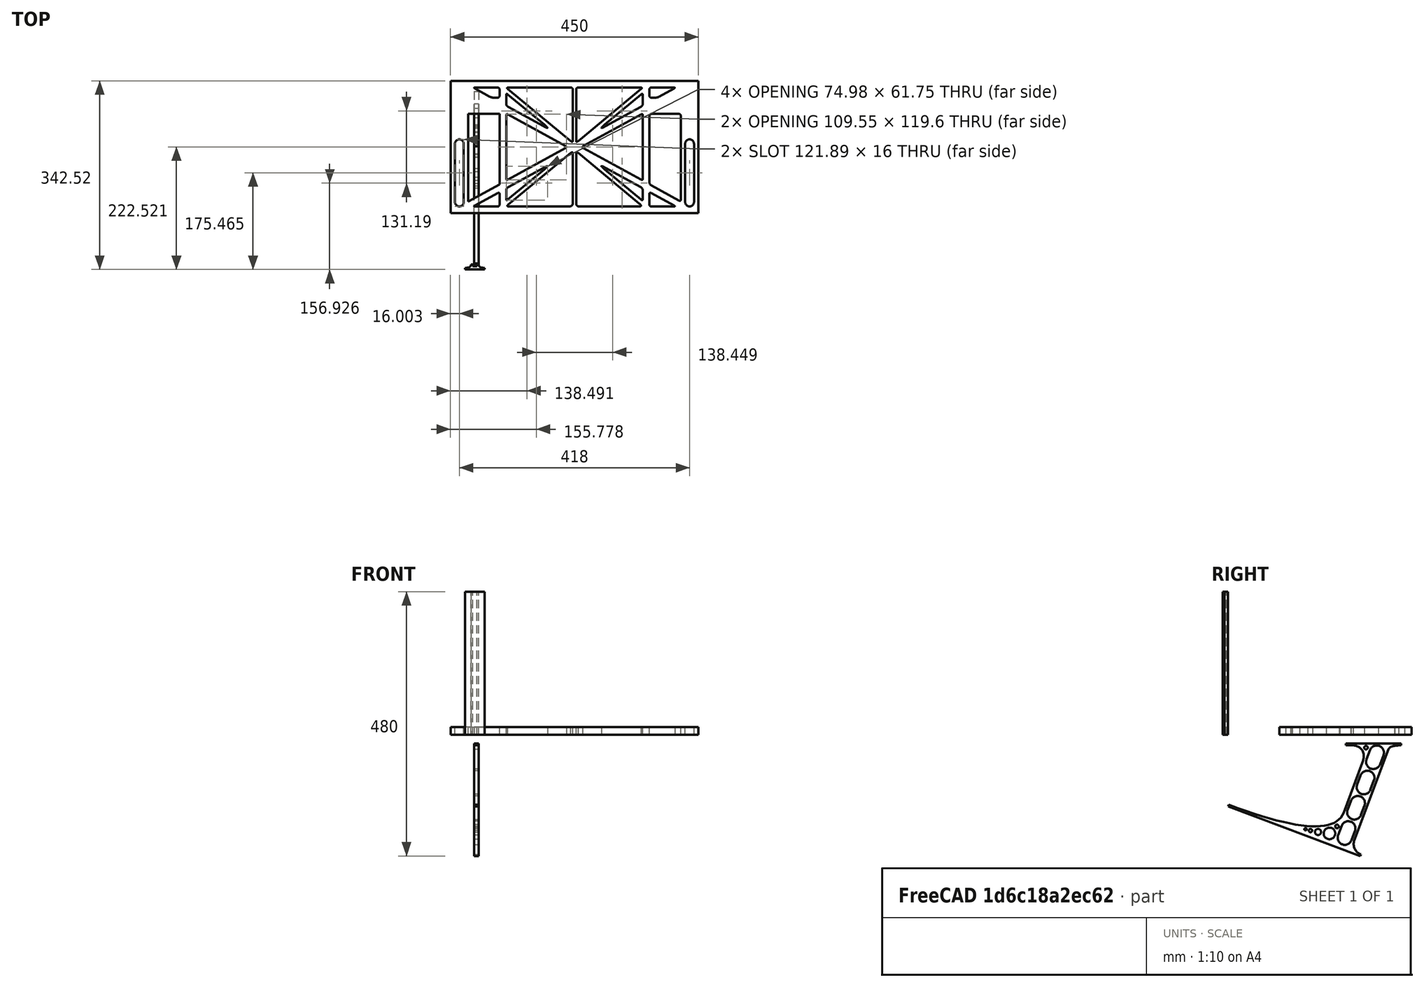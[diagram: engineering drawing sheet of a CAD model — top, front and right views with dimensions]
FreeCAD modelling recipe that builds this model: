
FCSTD DOCUMENT  (FreeCAD 0.19R0.19.2)
Label: laptopStand136FCStd
License: All rights reserved
LicenseURL: http://en.wikipedia.org/wiki/All_rights_reserved
objects: Sketcher::SketchObject×3, Part::Extrusion×3
note: 6 computed .brp shape members not serialized (recipe doc carries the construction recipe); baked Part::Feature solids carry a one-line shape summary decoded from their .brp

FEATURE [Sketcher::SketchObject] Sketch
  FullyConstrained = false
  sketch-geometry (352):
    g0: LineSegment StartX=-10.9272 StartY=-82.7794 StartZ=0 EndX=46.0728 EndY=-51.4823 EndZ=0
    g1: LineSegment StartX=-10.9272 StartY=76.4095 StartZ=0 EndX=-10.9272 EndY=-82.7794 EndZ=0
    g2: LineSegment StartX=46.0728 StartY=76.4095 StartZ=0 EndX=46.0728 EndY=-51.4823 EndZ=0
    g3: LineSegment StartX=-42.9272 StartY=136.221 StartZ=0 EndX=-42.9272 EndY=-103.779 EndZ=0
    g4: LineSegment StartX=407.073 StartY=136.221 StartZ=0 EndX=407.073 EndY=-103.779 EndZ=0
    g5: ArcOfCircle CenterX=-26.9272 CenterY=22.1087 CenterZ=0 NormalX=0 NormalY=0 NormalZ=1 AngleXU=0 Radius=8 StartAngle=3e-16 EndAngle=3.14159
    g6: ArcOfCircle CenterX=-26.9272 CenterY=-83.7794 CenterZ=0 NormalX=0 NormalY=0 NormalZ=1 AngleXU=0 Radius=8 StartAngle=3.14159 EndAngle=6.28319
    g7: LineSegment StartX=-34.9272 StartY=22.1087 StartZ=0 EndX=-34.9272 EndY=-83.7794 EndZ=0
    g8: LineSegment StartX=-18.9272 StartY=22.1087 StartZ=0 EndX=-18.9272 EndY=-83.7794 EndZ=0
    g9: ArcOfCircle CenterX=391.073 CenterY=22.1087 CenterZ=0 NormalX=0 NormalY=0 NormalZ=1 AngleXU=0 Radius=8 StartAngle=-4.4e-15 EndAngle=3.14159
    g10: LineSegment StartX=399.073 StartY=22.1087 StartZ=0 EndX=399.073 EndY=-83.7794 EndZ=0
    g11: LineSegment StartX=383.073 StartY=22.1087 StartZ=0 EndX=383.073 EndY=-83.7794 EndZ=0
    g12: ArcOfCircle CenterX=391.073 CenterY=-83.7794 CenterZ=0 NormalX=0 NormalY=0 NormalZ=1 AngleXU=0 Radius=8 StartAngle=3.14159 EndAngle=6.28319
    g13: Circle CenterX=175.022 CenterY=27.0628 CenterZ=0 NormalX=0 NormalY=0 NormalZ=1 AngleXU=0 Radius=1
    g14: Circle CenterX=179.022 CenterY=24.8665 CenterZ=0 NormalX=0 NormalY=0 NormalZ=1 AngleXU=0 Radius=1
    g15: Circle CenterX=179.022 CenterY=27.0628 CenterZ=0 NormalX=0 NormalY=0 NormalZ=1 AngleXU=0 Radius=1
    g16: BSplineCurve PolesCount=3 KnotsCount=2 Degree=2 IsPeriodic=0
    g17: GeomPoint X=175.022 Y=27.0628 Z=0
    g18: GeomPoint X=179.022 Y=27.0628 Z=0
    g19: Circle CenterX=189.124 CenterY=27.0628 CenterZ=0 NormalX=0 NormalY=0 NormalZ=1 AngleXU=0 Radius=1
    g20: Circle CenterX=185.124 CenterY=24.8665 CenterZ=0 NormalX=0 NormalY=0 NormalZ=1 AngleXU=0 Radius=1
    g21: Circle CenterX=185.124 CenterY=27.0628 CenterZ=0 NormalX=0 NormalY=0 NormalZ=1 AngleXU=0 Radius=1
    g22: BSplineCurve PolesCount=3 KnotsCount=2 Degree=2 IsPeriodic=0
    g23: GeomPoint X=189.124 Y=27.0628 Z=0
    g24: GeomPoint X=185.124 Y=27.0628 Z=0
    g25: Circle CenterX=175.022 CenterY=5.37834 CenterZ=0 NormalX=0 NormalY=0 NormalZ=1 AngleXU=0 Radius=1
    g26: Circle CenterX=179.022 CenterY=7.57463 CenterZ=0 NormalX=0 NormalY=0 NormalZ=1 AngleXU=0 Radius=1
    g27: Circle CenterX=179.022 CenterY=5.34704 CenterZ=0 NormalX=0 NormalY=0 NormalZ=1 AngleXU=0 Radius=1
    g28: BSplineCurve PolesCount=3 KnotsCount=2 Degree=2 IsPeriodic=0
    g29: GeomPoint X=175.022 Y=5.37834 Z=0
    g30: GeomPoint X=179.022 Y=5.34704 Z=0
    g31: Circle CenterX=189.124 CenterY=5.37834 CenterZ=0 NormalX=0 NormalY=0 NormalZ=1 AngleXU=0 Radius=1
    g32: Circle CenterX=185.124 CenterY=7.57463 CenterZ=0 NormalX=0 NormalY=0 NormalZ=1 AngleXU=0 Radius=1
    g33: Circle CenterX=185.124 CenterY=5.34704 CenterZ=0 NormalX=0 NormalY=0 NormalZ=1 AngleXU=0 Radius=1
    g34: BSplineCurve PolesCount=3 KnotsCount=2 Degree=2 IsPeriodic=0
    g35: GeomPoint X=189.124 Y=5.37834 Z=0
    g36: GeomPoint X=185.124 Y=5.34704 Z=0
    g37: Circle CenterX=165.871 CenterY=18.1458 CenterZ=0 NormalX=0 NormalY=0 NormalZ=1 AngleXU=0 Radius=1
    g38: Circle CenterX=169.377 CenterY=16.2206 CenterZ=0 NormalX=0 NormalY=0 NormalZ=1 AngleXU=0 Radius=1
    g39: Circle CenterX=165.871 CenterY=14.2954 CenterZ=0 NormalX=0 NormalY=0 NormalZ=1 AngleXU=0 Radius=1
    g40: BSplineCurve PolesCount=3 KnotsCount=2 Degree=2 IsPeriodic=0
    g41: GeomPoint X=165.871 Y=18.1458 Z=0
    g42: GeomPoint X=165.871 Y=14.2954 Z=0
    g43: Circle CenterX=198.275 CenterY=18.1458 CenterZ=0 NormalX=0 NormalY=0 NormalZ=1 AngleXU=0 Radius=1
    g44: Circle CenterX=194.768 CenterY=16.2206 CenterZ=0 NormalX=0 NormalY=0 NormalZ=1 AngleXU=0 Radius=1
    g45: Circle CenterX=198.275 CenterY=14.2954 CenterZ=0 NormalX=0 NormalY=0 NormalZ=1 AngleXU=0 Radius=1
    g46: BSplineCurve PolesCount=3 KnotsCount=2 Degree=2 IsPeriodic=0
    g47: GeomPoint X=198.275 Y=18.1458 Z=0
    g48: GeomPoint X=198.275 Y=14.2954 Z=0
    g49: LineSegment StartX=407.073 StartY=-103.779 StartZ=0 EndX=-42.9272 EndY=-103.779 EndZ=0
    g50: LineSegment StartX=407.073 StartY=136.221 StartZ=0 EndX=-42.9272 EndY=136.221 EndZ=0
    g51: LineSegment StartX=46.0728 StartY=76.4095 StartZ=0 EndX=-10.9272 EndY=76.4095 EndZ=0
    g52: Circle CenterX=125.607 CenterY=54.1951 CenterZ=0 NormalX=0 NormalY=0 NormalZ=1 AngleXU=0 Radius=1
    g53: Circle CenterX=139.632 CenterY=46.4944 CenterZ=0 NormalX=0 NormalY=0 NormalZ=1 AngleXU=0 Radius=1
    g54: Circle CenterX=127.326 CenterY=56.7187 CenterZ=0 NormalX=0 NormalY=0 NormalZ=1 AngleXU=0 Radius=1
    g55: BSplineCurve PolesCount=3 KnotsCount=2 Degree=2 IsPeriodic=0
    g56: GeomPoint X=125.607 Y=54.1951 Z=0
    g57: GeomPoint X=127.326 Y=56.7187 Z=0
    g58: Circle CenterX=236.821 CenterY=56.7187 CenterZ=0 NormalX=0 NormalY=0 NormalZ=1 AngleXU=0 Radius=1
    g59: Circle CenterX=224.513 CenterY=46.4944 CenterZ=0 NormalX=0 NormalY=0 NormalZ=1 AngleXU=0 Radius=1
    g60: Circle CenterX=238.538 CenterY=54.1951 CenterZ=0 NormalX=0 NormalY=0 NormalZ=1 AngleXU=0 Radius=1
    g61: BSplineCurve PolesCount=3 KnotsCount=2 Degree=2 IsPeriodic=0
    g62: GeomPoint X=236.821 Y=56.7187 Z=0
    g63: GeomPoint X=238.538 Y=54.1951 Z=0
    g64: Circle CenterX=238.538 CenterY=-21.7539 CenterZ=0 NormalX=0 NormalY=0 NormalZ=1 AngleXU=0 Radius=1
    g65: Circle CenterX=224.513 CenterY=-14.0532 CenterZ=0 NormalX=0 NormalY=0 NormalZ=1 AngleXU=0 Radius=1
    g66: Circle CenterX=236.821 CenterY=-24.2775 CenterZ=0 NormalX=0 NormalY=0 NormalZ=1 AngleXU=0 Radius=1
    g67: BSplineCurve PolesCount=3 KnotsCount=2 Degree=2 IsPeriodic=0
    g68: GeomPoint X=238.538 Y=-21.7539 Z=0
    g69: GeomPoint X=236.821 Y=-24.2775 Z=0
    g70: Circle CenterX=125.607 CenterY=-21.7539 CenterZ=0 NormalX=0 NormalY=0 NormalZ=1 AngleXU=0 Radius=1
    g71: Circle CenterX=139.632 CenterY=-14.0532 CenterZ=0 NormalX=0 NormalY=0 NormalZ=1 AngleXU=0 Radius=1
    g72: Circle CenterX=127.325 CenterY=-24.2775 CenterZ=0 NormalX=0 NormalY=0 NormalZ=1 AngleXU=0 Radius=1
    g73: BSplineCurve PolesCount=3 KnotsCount=2 Degree=2 IsPeriodic=0
    g74: GeomPoint X=125.607 Y=-21.7539 Z=0
    g75: GeomPoint X=127.325 Y=-24.2775 Z=0
    g76: Circle CenterX=302.996 CenterY=111.695 CenterZ=0 NormalX=0 NormalY=0 NormalZ=1 AngleXU=0 Radius=1
    g77: Circle CenterX=306.073 CenterY=114.251 CenterZ=0 NormalX=0 NormalY=0 NormalZ=1 AngleXU=0 Radius=1
    g78: Circle CenterX=306.073 CenterY=110.251 CenterZ=0 NormalX=0 NormalY=0 NormalZ=1 AngleXU=0 Radius=1
    g79: BSplineCurve PolesCount=3 KnotsCount=2 Degree=2 IsPeriodic=0
    g80: GeomPoint X=302.996 Y=111.695 Z=0
    g81: GeomPoint X=306.073 Y=110.251 Z=0
    g82: Circle CenterX=306.073 CenterY=95.2763 CenterZ=0 NormalX=0 NormalY=0 NormalZ=1 AngleXU=0 Radius=1
    g83: Circle CenterX=306.073 CenterY=91.2763 CenterZ=0 NormalX=0 NormalY=0 NormalZ=1 AngleXU=0 Radius=1
    g84: Circle CenterX=302.567 CenterY=89.3511 CenterZ=0 NormalX=0 NormalY=0 NormalZ=1 AngleXU=0 Radius=1
    g85: BSplineCurve PolesCount=3 KnotsCount=2 Degree=2 IsPeriodic=0
    g86: GeomPoint X=306.073 Y=95.2763 Z=0
    g87: GeomPoint X=302.567 Y=89.3511 Z=0
    g88: LineSegment StartX=306.073 StartY=110.251 StartZ=0 EndX=306.073 EndY=95.2763 EndZ=0
    g89: LineSegment StartX=302.996 StartY=111.695 StartZ=0 EndX=236.821 EndY=56.7187 EndZ=0
    g90: LineSegment StartX=238.538 StartY=54.1951 StartZ=0 EndX=302.567 EndY=89.3511 EndZ=0
    g91: Circle CenterX=61.1496 CenterY=111.695 CenterZ=0 NormalX=0 NormalY=0 NormalZ=1 AngleXU=0 Radius=1
    g92: Circle CenterX=58.0728 CenterY=114.251 CenterZ=0 NormalX=0 NormalY=0 NormalZ=1 AngleXU=0 Radius=1
    g93: Circle CenterX=58.0728 CenterY=110.251 CenterZ=0 NormalX=0 NormalY=0 NormalZ=1 AngleXU=0 Radius=1
    g94: BSplineCurve PolesCount=3 KnotsCount=2 Degree=2 IsPeriodic=0
    g95: GeomPoint X=61.1496 Y=111.695 Z=0
    g96: GeomPoint X=58.0728 Y=110.251 Z=0
    g97: Circle CenterX=61.5791 CenterY=89.3511 CenterZ=0 NormalX=0 NormalY=0 NormalZ=1 AngleXU=0 Radius=1
    g98: Circle CenterX=58.0728 CenterY=91.2763 CenterZ=0 NormalX=0 NormalY=0 NormalZ=1 AngleXU=0 Radius=1
    g99: Circle CenterX=58.0728 CenterY=95.2763 CenterZ=0 NormalX=0 NormalY=0 NormalZ=1 AngleXU=0 Radius=1
    g100: BSplineCurve PolesCount=3 KnotsCount=2 Degree=2 IsPeriodic=0
    g101: GeomPoint X=61.5791 Y=89.3511 Z=0
    g102: GeomPoint X=58.0728 Y=95.2763 Z=0
    g103: LineSegment StartX=58.0728 StartY=110.251 StartZ=0 EndX=58.0728 EndY=95.2763 EndZ=0
    g104: LineSegment StartX=61.1496 StartY=111.695 StartZ=0 EndX=127.326 EndY=56.7187 EndZ=0
    g105: LineSegment StartX=125.607 StartY=54.1951 StartZ=0 EndX=61.5791 EndY=89.3511 EndZ=0
    g106: Circle CenterX=61.5791 CenterY=-56.9099 CenterZ=0 NormalX=0 NormalY=0 NormalZ=1 AngleXU=0 Radius=1
    g107: Circle CenterX=58.0728 CenterY=-58.8351 CenterZ=0 NormalX=0 NormalY=0 NormalZ=1 AngleXU=0 Radius=1
    g108: Circle CenterX=58.0728 CenterY=-62.8351 CenterZ=0 NormalX=0 NormalY=0 NormalZ=1 AngleXU=0 Radius=1
    g109: BSplineCurve PolesCount=3 KnotsCount=2 Degree=2 IsPeriodic=0
    g110: GeomPoint X=61.5791 Y=-56.9099 Z=0
    g111: GeomPoint X=58.0728 Y=-62.8351 Z=0
    g112: Circle CenterX=58.0728 CenterY=-77.8102 CenterZ=0 NormalX=0 NormalY=0 NormalZ=1 AngleXU=0 Radius=1
    g113: Circle CenterX=58.0728 CenterY=-81.8102 CenterZ=0 NormalX=0 NormalY=0 NormalZ=1 AngleXU=0 Radius=1
    g114: Circle CenterX=61.1496 CenterY=-79.2541 CenterZ=0 NormalX=0 NormalY=0 NormalZ=1 AngleXU=0 Radius=1
    g115: BSplineCurve PolesCount=3 KnotsCount=2 Degree=2 IsPeriodic=0
    g116: GeomPoint X=58.0728 Y=-77.8102 Z=0
    g117: GeomPoint X=61.1496 Y=-79.2541 Z=0
    g118: LineSegment StartX=58.0728 StartY=-62.8351 StartZ=0 EndX=58.0728 EndY=-77.8102 EndZ=0
    g119: LineSegment StartX=61.1496 StartY=-79.2541 StartZ=0 EndX=127.325 EndY=-24.2775 EndZ=0
    g120: LineSegment StartX=125.607 StartY=-21.7539 StartZ=0 EndX=61.5791 EndY=-56.9099 EndZ=0
    g121: Circle CenterX=302.567 CenterY=-56.9099 CenterZ=0 NormalX=0 NormalY=0 NormalZ=1 AngleXU=0 Radius=1
    g122: Circle CenterX=306.073 CenterY=-58.8351 CenterZ=0 NormalX=0 NormalY=0 NormalZ=1 AngleXU=0 Radius=1
    g123: Circle CenterX=306.073 CenterY=-62.8351 CenterZ=0 NormalX=0 NormalY=0 NormalZ=1 AngleXU=0 Radius=1
    g124: BSplineCurve PolesCount=3 KnotsCount=2 Degree=2 IsPeriodic=0
    g125: GeomPoint X=302.567 Y=-56.9099 Z=0
    g126: GeomPoint X=306.073 Y=-62.8351 Z=0
    g127: Circle CenterX=302.996 CenterY=-79.2541 CenterZ=0 NormalX=0 NormalY=0 NormalZ=1 AngleXU=0 Radius=1
    g128: Circle CenterX=306.073 CenterY=-81.8102 CenterZ=0 NormalX=0 NormalY=0 NormalZ=1 AngleXU=0 Radius=1
    g129: Circle CenterX=306.073 CenterY=-77.8102 CenterZ=0 NormalX=0 NormalY=0 NormalZ=1 AngleXU=0 Radius=1
    g130: BSplineCurve PolesCount=3 KnotsCount=2 Degree=2 IsPeriodic=0
    g131: GeomPoint X=302.996 Y=-79.2541 Z=0
    g132: GeomPoint X=306.073 Y=-77.8102 Z=0
    g133: LineSegment StartX=306.073 StartY=-62.8351 StartZ=0 EndX=306.073 EndY=-77.8102 EndZ=0
    g134: LineSegment StartX=302.996 StartY=-79.2541 StartZ=0 EndX=236.821 EndY=-24.2775 EndZ=0
    g135: LineSegment StartX=238.538 StartY=-21.7539 StartZ=0 EndX=302.567 EndY=-56.9099 EndZ=0
    g136: Circle CenterX=61.6457 CenterY=-88.8112 CenterZ=0 NormalX=0 NormalY=0 NormalZ=1 AngleXU=0 Radius=1
    g137: Circle CenterX=58.0728 CenterY=-91.7794 CenterZ=0 NormalX=0 NormalY=0 NormalZ=1 AngleXU=0 Radius=1
    g138: Circle CenterX=63.9135 CenterY=-91.7794 CenterZ=0 NormalX=0 NormalY=0 NormalZ=1 AngleXU=0 Radius=1
    g139: BSplineCurve PolesCount=3 KnotsCount=2 Degree=2 IsPeriodic=0
    g140: GeomPoint X=61.6457 Y=-88.8112 Z=0
    g141: GeomPoint X=63.9135 Y=-91.7794 Z=0
    g142: Circle CenterX=179.022 CenterY=-85.8163 CenterZ=0 NormalX=0 NormalY=0 NormalZ=1 AngleXU=0 Radius=1
    g143: Circle CenterX=179.022 CenterY=-91.7794 CenterZ=0 NormalX=0 NormalY=0 NormalZ=1 AngleXU=0 Radius=1
    g144: Circle CenterX=171.895 CenterY=-91.7794 CenterZ=0 NormalX=0 NormalY=0 NormalZ=1 AngleXU=0 Radius=1
    g145: BSplineCurve PolesCount=3 KnotsCount=2 Degree=2 IsPeriodic=0
    g146: GeomPoint X=179.022 Y=-85.8163 Z=0
    g147: GeomPoint X=171.895 Y=-91.7794 Z=0
    g148: Circle CenterX=185.124 CenterY=-86.2028 CenterZ=0 NormalX=0 NormalY=0 NormalZ=1 AngleXU=0 Radius=1
    g149: Circle CenterX=185.124 CenterY=-91.7794 CenterZ=0 NormalX=0 NormalY=0 NormalZ=1 AngleXU=0 Radius=1
    g150: Circle CenterX=191.747 CenterY=-91.7794 CenterZ=0 NormalX=0 NormalY=0 NormalZ=1 AngleXU=0 Radius=1
    g151: BSplineCurve PolesCount=3 KnotsCount=2 Degree=2 IsPeriodic=0
    g152: GeomPoint X=185.124 Y=-86.2028 Z=0
    g153: GeomPoint X=191.747 Y=-91.7794 Z=0
    g154: Circle CenterX=299.888 CenterY=-86.6413 CenterZ=0 NormalX=0 NormalY=0 NormalZ=1 AngleXU=0 Radius=1
    g155: Circle CenterX=306.073 CenterY=-91.7794 CenterZ=0 NormalX=0 NormalY=0 NormalZ=1 AngleXU=0 Radius=1
    g156: Circle CenterX=298.776 CenterY=-91.7794 CenterZ=0 NormalX=0 NormalY=0 NormalZ=1 AngleXU=0 Radius=1
    g157: BSplineCurve PolesCount=3 KnotsCount=2 Degree=2 IsPeriodic=0
    g158: GeomPoint X=299.888 Y=-86.6413 Z=0
    g159: GeomPoint X=298.776 Y=-91.7794 Z=0
    g160: LineSegment StartX=189.124 StartY=5.37834 StartZ=0 EndX=299.888 EndY=-86.6413 EndZ=0
    g161: LineSegment StartX=298.776 StartY=-91.7794 StartZ=0 EndX=191.747 EndY=-91.7794 EndZ=0
    g162: LineSegment StartX=185.124 StartY=-86.2028 StartZ=0 EndX=185.124 EndY=5.34704 EndZ=0
    g163: LineSegment StartX=179.022 StartY=5.34704 StartZ=0 EndX=179.022 EndY=-85.8163 EndZ=0
    g164: LineSegment StartX=171.895 StartY=-91.7794 StartZ=0 EndX=63.9135 EndY=-91.7794 EndZ=0
    g165: LineSegment StartX=61.6457 StartY=-88.8112 StartZ=0 EndX=175.022 EndY=5.37834 EndZ=0
    g166: Circle CenterX=302.073 CenterY=124.221 CenterZ=0 NormalX=0 NormalY=0 NormalZ=1 AngleXU=0 Radius=1
    g167: Circle CenterX=306.073 CenterY=124.221 CenterZ=0 NormalX=0 NormalY=0 NormalZ=1 AngleXU=0 Radius=1
    g168: Circle CenterX=302.996 CenterY=121.665 CenterZ=0 NormalX=0 NormalY=0 NormalZ=1 AngleXU=0 Radius=1
    g169: BSplineCurve PolesCount=3 KnotsCount=2 Degree=2 IsPeriodic=0
    g170: GeomPoint X=302.073 Y=124.221 Z=0
    g171: GeomPoint X=302.996 Y=121.665 Z=0
    g172: Circle CenterX=189.124 CenterY=124.221 CenterZ=0 NormalX=0 NormalY=0 NormalZ=1 AngleXU=0 Radius=1
    g173: Circle CenterX=185.124 CenterY=124.221 CenterZ=0 NormalX=0 NormalY=0 NormalZ=1 AngleXU=0 Radius=1
    g174: Circle CenterX=185.124 CenterY=120.221 CenterZ=0 NormalX=0 NormalY=0 NormalZ=1 AngleXU=0 Radius=1
    g175: BSplineCurve PolesCount=3 KnotsCount=2 Degree=2 IsPeriodic=0
    g176: GeomPoint X=189.124 Y=124.221 Z=0
    g177: GeomPoint X=185.124 Y=120.221 Z=0
    g178: Circle CenterX=175.022 CenterY=124.221 CenterZ=0 NormalX=0 NormalY=0 NormalZ=1 AngleXU=0 Radius=1
    g179: Circle CenterX=179.022 CenterY=124.221 CenterZ=0 NormalX=0 NormalY=0 NormalZ=1 AngleXU=0 Radius=1
    g180: Circle CenterX=179.022 CenterY=120.221 CenterZ=0 NormalX=0 NormalY=0 NormalZ=1 AngleXU=0 Radius=1
    g181: BSplineCurve PolesCount=3 KnotsCount=2 Degree=2 IsPeriodic=0
    g182: GeomPoint X=175.022 Y=124.221 Z=0
    g183: GeomPoint X=179.022 Y=120.221 Z=0
    g184: Circle CenterX=62.0728 CenterY=124.221 CenterZ=0 NormalX=0 NormalY=0 NormalZ=1 AngleXU=0 Radius=1
    g185: Circle CenterX=58.0728 CenterY=124.221 CenterZ=0 NormalX=0 NormalY=0 NormalZ=1 AngleXU=0 Radius=1
    g186: Circle CenterX=61.1496 CenterY=121.665 CenterZ=0 NormalX=0 NormalY=0 NormalZ=1 AngleXU=0 Radius=1
    g187: BSplineCurve PolesCount=3 KnotsCount=2 Degree=2 IsPeriodic=0
    g188: GeomPoint X=62.0728 Y=124.221 Z=0
    g189: GeomPoint X=61.1496 Y=121.665 Z=0
    g190: LineSegment StartX=62.0728 StartY=124.221 StartZ=0 EndX=175.022 EndY=124.221 EndZ=0
    g191: LineSegment StartX=179.022 StartY=120.221 StartZ=0 EndX=179.022 EndY=27.0628 EndZ=0
    g192: LineSegment StartX=185.124 StartY=27.0628 StartZ=0 EndX=185.124 EndY=120.221 EndZ=0
    g193: LineSegment StartX=189.124 StartY=124.221 StartZ=0 EndX=302.073 EndY=124.221 EndZ=0
    g194: LineSegment StartX=302.996 StartY=121.665 StartZ=0 EndX=189.124 EndY=27.0628 EndZ=0
    g195: LineSegment StartX=175.022 StartY=27.0628 StartZ=0 EndX=61.1496 EndY=121.665 EndZ=0
    g196: Circle CenterX=61.5791 CenterY=75.4095 CenterZ=0 NormalX=0 NormalY=0 NormalZ=1 AngleXU=0 Radius=1
    g197: Circle CenterX=58.0728 CenterY=77.3346 CenterZ=0 NormalX=0 NormalY=0 NormalZ=1 AngleXU=0 Radius=1
    g198: Circle CenterX=58.0728 CenterY=73.3346 CenterZ=0 NormalX=0 NormalY=0 NormalZ=1 AngleXU=0 Radius=1
    g199: BSplineCurve PolesCount=3 KnotsCount=2 Degree=2 IsPeriodic=0
    g200: GeomPoint X=61.5791 Y=75.4095 Z=0
    g201: GeomPoint X=58.0728 Y=73.3346 Z=0
    g202: Circle CenterX=58.0728 CenterY=-40.8935 CenterZ=0 NormalX=0 NormalY=0 NormalZ=1 AngleXU=0 Radius=1
    g203: Circle CenterX=58.0728 CenterY=-44.8935 CenterZ=0 NormalX=0 NormalY=0 NormalZ=1 AngleXU=0 Radius=1
    g204: Circle CenterX=61.5791 CenterY=-42.9683 CenterZ=0 NormalX=0 NormalY=0 NormalZ=1 AngleXU=0 Radius=1
    g205: BSplineCurve PolesCount=3 KnotsCount=2 Degree=2 IsPeriodic=0
    g206: GeomPoint X=58.0728 Y=-40.8935 Z=0
    g207: GeomPoint X=61.5791 Y=-42.9683 Z=0
    g208: LineSegment StartX=61.5791 StartY=-42.9683 StartZ=0 EndX=165.871 EndY=14.2954 EndZ=0
    g209: LineSegment StartX=165.871 StartY=18.1458 StartZ=0 EndX=61.5791 EndY=75.4095 EndZ=0
    g210: LineSegment StartX=58.0728 StartY=73.3346 StartZ=0 EndX=58.0728 EndY=-40.8935 EndZ=0
    g211: Circle CenterX=302.567 CenterY=-42.9683 CenterZ=0 NormalX=0 NormalY=0 NormalZ=1 AngleXU=0 Radius=1
    g212: Circle CenterX=306.073 CenterY=-44.8935 CenterZ=0 NormalX=0 NormalY=0 NormalZ=1 AngleXU=0 Radius=1
    g213: Circle CenterX=306.073 CenterY=-40.8935 CenterZ=0 NormalX=0 NormalY=0 NormalZ=1 AngleXU=0 Radius=1
    g214: BSplineCurve PolesCount=3 KnotsCount=2 Degree=2 IsPeriodic=0
    g215: GeomPoint X=302.567 Y=-42.9683 Z=0
    g216: GeomPoint X=306.073 Y=-40.8935 Z=0
    g217: Circle CenterX=306.073 CenterY=73.3346 CenterZ=0 NormalX=0 NormalY=0 NormalZ=1 AngleXU=0 Radius=1
    g218: Circle CenterX=306.073 CenterY=77.3346 CenterZ=0 NormalX=0 NormalY=0 NormalZ=1 AngleXU=0 Radius=1
    g219: Circle CenterX=302.567 CenterY=75.4095 CenterZ=0 NormalX=0 NormalY=0 NormalZ=1 AngleXU=0 Radius=1
    g220: BSplineCurve PolesCount=3 KnotsCount=2 Degree=2 IsPeriodic=0
    g221: GeomPoint X=306.073 Y=73.3346 Z=0
    g222: GeomPoint X=302.567 Y=75.4095 Z=0
    g223: LineSegment StartX=302.567 StartY=-42.9683 StartZ=0 EndX=198.275 EndY=14.2954 EndZ=0
    g224: LineSegment StartX=198.275 StartY=18.1458 StartZ=0 EndX=302.567 EndY=75.4095 EndZ=0
    g225: LineSegment StartX=306.073 StartY=73.3346 StartZ=0 EndX=306.073 EndY=-40.8935 EndZ=0
    g226: LineSegment StartX=322.073 StartY=105.865 StartZ=0 EndX=328.643 EndY=105.865 EndZ=0
    g227: LineSegment StartX=318.073 StartY=120.221 StartZ=0 EndX=318.073 EndY=109.865 EndZ=0
    g228: LineSegment StartX=336.157 StartY=107.779 StartZ=0 EndX=362.567 EndY=122.294 EndZ=0
    g229: Circle CenterX=362.073 CenterY=124.221 CenterZ=0 NormalX=0 NormalY=0 NormalZ=1 AngleXU=0 Radius=1
    g230: Circle CenterX=366.073 CenterY=124.221 CenterZ=0 NormalX=0 NormalY=0 NormalZ=1 AngleXU=0 Radius=1
    g231: Circle CenterX=362.567 CenterY=122.294 CenterZ=0 NormalX=0 NormalY=0 NormalZ=1 AngleXU=0 Radius=1
    g232: BSplineCurve PolesCount=3 KnotsCount=2 Degree=2 IsPeriodic=0
    g233: GeomPoint X=362.073 Y=124.221 Z=0
    g234: GeomPoint X=362.567 Y=122.294 Z=0
    g235: Circle CenterX=322.073 CenterY=124.221 CenterZ=0 NormalX=0 NormalY=0 NormalZ=1 AngleXU=0 Radius=1
    g236: Circle CenterX=318.073 CenterY=124.221 CenterZ=0 NormalX=0 NormalY=0 NormalZ=1 AngleXU=0 Radius=1
    g237: Circle CenterX=318.073 CenterY=120.221 CenterZ=0 NormalX=0 NormalY=0 NormalZ=1 AngleXU=0 Radius=1
    g238: BSplineCurve PolesCount=3 KnotsCount=2 Degree=2 IsPeriodic=0
    g239: GeomPoint X=322.073 Y=124.221 Z=0
    g240: GeomPoint X=318.073 Y=120.221 Z=0
    g241: Circle CenterX=322.073 CenterY=105.865 CenterZ=0 NormalX=0 NormalY=0 NormalZ=1 AngleXU=0 Radius=1
    g242: Circle CenterX=318.073 CenterY=105.865 CenterZ=0 NormalX=0 NormalY=0 NormalZ=1 AngleXU=0 Radius=1
    g243: Circle CenterX=318.073 CenterY=109.865 CenterZ=0 NormalX=0 NormalY=0 NormalZ=1 AngleXU=0 Radius=1
    g244: BSplineCurve PolesCount=3 KnotsCount=2 Degree=2 IsPeriodic=0
    g245: GeomPoint X=322.073 Y=105.865 Z=0
    g246: GeomPoint X=318.073 Y=109.865 Z=0
    g247: Circle CenterX=336.157 CenterY=107.779 CenterZ=0 NormalX=0 NormalY=0 NormalZ=1 AngleXU=0 Radius=1
    g248: Circle CenterX=332.651 CenterY=105.853 CenterZ=0 NormalX=0 NormalY=0 NormalZ=1 AngleXU=0 Radius=1
    g249: Circle CenterX=328.643 CenterY=105.865 CenterZ=0 NormalX=0 NormalY=0 NormalZ=1 AngleXU=0 Radius=1
    g250: BSplineCurve PolesCount=3 KnotsCount=2 Degree=2 IsPeriodic=0
    g251: GeomPoint X=336.157 Y=107.779 Z=0
    g252: GeomPoint X=328.643 Y=105.865 Z=0
    g253: LineSegment StartX=322.073 StartY=124.221 StartZ=0 EndX=362.073 EndY=124.221 EndZ=0
    g254: Circle CenterX=371.567 CenterY=-80.8644 CenterZ=0 NormalX=0 NormalY=0 NormalZ=1 AngleXU=0 Radius=1
    g255: Circle CenterX=375.073 CenterY=-82.7896 CenterZ=0 NormalX=0 NormalY=0 NormalZ=1 AngleXU=0 Radius=1
    g256: Circle CenterX=375.073 CenterY=-78.7896 CenterZ=0 NormalX=0 NormalY=0 NormalZ=1 AngleXU=0 Radius=1
    g257: BSplineCurve PolesCount=3 KnotsCount=2 Degree=2 IsPeriodic=0
    g258: GeomPoint X=371.567 Y=-80.8644 Z=0
    g259: GeomPoint X=375.073 Y=-78.7896 Z=0
    g260: Circle CenterX=321.579 CenterY=-53.4075 CenterZ=0 NormalX=0 NormalY=0 NormalZ=1 AngleXU=0 Radius=1
    g261: Circle CenterX=318.073 CenterY=-51.4823 CenterZ=0 NormalX=0 NormalY=0 NormalZ=1 AngleXU=0 Radius=1
    g262: Circle CenterX=318.073 CenterY=-47.4823 CenterZ=0 NormalX=0 NormalY=0 NormalZ=1 AngleXU=0 Radius=1
    g263: BSplineCurve PolesCount=3 KnotsCount=2 Degree=2 IsPeriodic=0
    g264: GeomPoint X=321.579 Y=-53.4075 Z=0
    g265: GeomPoint X=318.073 Y=-47.4823 Z=0
    g266: LineSegment StartX=371.567 StartY=-80.8644 StartZ=0 EndX=321.579 EndY=-53.4075 EndZ=0
    g267: Circle CenterX=321.579 CenterY=-67.3492 CenterZ=0 NormalX=0 NormalY=0 NormalZ=1 AngleXU=0 Radius=1
    g268: Circle CenterX=318.073 CenterY=-65.424 CenterZ=0 NormalX=0 NormalY=0 NormalZ=1 AngleXU=0 Radius=1
    g269: Circle CenterX=318.073 CenterY=-69.424 CenterZ=0 NormalX=0 NormalY=0 NormalZ=1 AngleXU=0 Radius=1
    g270: BSplineCurve PolesCount=3 KnotsCount=2 Degree=2 IsPeriodic=0
    g271: GeomPoint X=321.579 Y=-67.3492 Z=0
    g272: GeomPoint X=318.073 Y=-69.424 Z=0
    g273: Circle CenterX=362.567 CenterY=-89.8542 CenterZ=0 NormalX=0 NormalY=0 NormalZ=1 AngleXU=0 Radius=1
    g274: Circle CenterX=366.073 CenterY=-91.7794 CenterZ=0 NormalX=0 NormalY=0 NormalZ=1 AngleXU=0 Radius=1
    g275: Circle CenterX=362.073 CenterY=-91.7794 CenterZ=0 NormalX=0 NormalY=0 NormalZ=1 AngleXU=0 Radius=1
    g276: BSplineCurve PolesCount=3 KnotsCount=2 Degree=2 IsPeriodic=0
    g277: GeomPoint X=362.567 Y=-89.8542 Z=0
    g278: GeomPoint X=362.073 Y=-91.7794 Z=0
    g279: Circle CenterX=322.073 CenterY=-91.7794 CenterZ=0 NormalX=0 NormalY=0 NormalZ=1 AngleXU=0 Radius=1
    g280: Circle CenterX=318.073 CenterY=-91.7794 CenterZ=0 NormalX=0 NormalY=0 NormalZ=1 AngleXU=0 Radius=1
    g281: Circle CenterX=318.073 CenterY=-87.7794 CenterZ=0 NormalX=0 NormalY=0 NormalZ=1 AngleXU=0 Radius=1
    g282: BSplineCurve PolesCount=3 KnotsCount=2 Degree=2 IsPeriodic=0
    g283: GeomPoint X=322.073 Y=-91.7794 Z=0
    g284: GeomPoint X=318.073 Y=-87.7794 Z=0
    g285: LineSegment StartX=362.567 StartY=-89.8542 StartZ=0 EndX=321.579 EndY=-67.3492 EndZ=0
    g286: LineSegment StartX=318.073 StartY=-69.424 StartZ=0 EndX=318.073 EndY=-87.7794 EndZ=0
    g287: LineSegment StartX=322.073 StartY=-91.7794 StartZ=0 EndX=362.073 EndY=-91.7794 EndZ=0
    g288: Circle CenterX=2.07281 CenterY=124.221 CenterZ=0 NormalX=0 NormalY=0 NormalZ=1 AngleXU=0 Radius=1
    g289: Circle CenterX=1.57905 CenterY=122.295 CenterZ=0 NormalX=0 NormalY=0 NormalZ=1 AngleXU=0 Radius=1
    g290: BSplineCurve PolesCount=3 KnotsCount=2 Degree=2 IsPeriodic=0
    g291: GeomPoint X=2.07281 Y=124.221 Z=0
    g292: GeomPoint X=1.57905 Y=122.295 Z=0
    g293: Circle CenterX=42.0728 CenterY=124.221 CenterZ=0 NormalX=0 NormalY=0 NormalZ=1 AngleXU=0 Radius=1
    g294: Circle CenterX=46.0728 CenterY=124.221 CenterZ=0 NormalX=0 NormalY=0 NormalZ=1 AngleXU=0 Radius=1
    g295: Circle CenterX=46.0728 CenterY=120.221 CenterZ=0 NormalX=0 NormalY=0 NormalZ=1 AngleXU=0 Radius=1
    g296: BSplineCurve PolesCount=3 KnotsCount=2 Degree=2 IsPeriodic=0
    g297: GeomPoint X=42.0728 Y=124.221 Z=0
    g298: GeomPoint X=46.0728 Y=120.221 Z=0
    g299: Circle CenterX=46.0728 CenterY=109.865 CenterZ=0 NormalX=0 NormalY=0 NormalZ=1 AngleXU=0 Radius=1
    g300: Circle CenterX=46.0728 CenterY=105.865 CenterZ=0 NormalX=0 NormalY=0 NormalZ=1 AngleXU=0 Radius=1
    g301: Circle CenterX=42.0728 CenterY=105.865 CenterZ=0 NormalX=0 NormalY=0 NormalZ=1 AngleXU=0 Radius=1
    g302: BSplineCurve PolesCount=3 KnotsCount=2 Degree=2 IsPeriodic=0
    g303: GeomPoint X=46.0728 Y=109.865 Z=0
    g304: GeomPoint X=42.0728 Y=105.865 Z=0
    g305: Circle CenterX=35.5028 CenterY=105.865 CenterZ=0 NormalX=0 NormalY=0 NormalZ=1 AngleXU=0 Radius=1
    g306: Circle CenterX=31.5028 CenterY=105.865 CenterZ=0 NormalX=0 NormalY=0 NormalZ=1 AngleXU=0 Radius=1
    g307: Circle CenterX=27.9965 CenterY=107.79 CenterZ=0 NormalX=0 NormalY=0 NormalZ=1 AngleXU=0 Radius=1
    g308: BSplineCurve PolesCount=3 KnotsCount=2 Degree=2 IsPeriodic=0
    g309: GeomPoint X=35.5028 Y=105.865 Z=0
    g310: GeomPoint X=27.9965 Y=107.79 Z=0
    g311: LineSegment StartX=2.07281 StartY=124.221 StartZ=0 EndX=42.0728 EndY=124.221 EndZ=0
    g312: LineSegment StartX=46.0728 StartY=120.221 StartZ=0 EndX=46.0728 EndY=109.865 EndZ=0
    g313: LineSegment StartX=42.0728 StartY=105.865 StartZ=0 EndX=35.5028 EndY=105.865 EndZ=0
    g314: LineSegment StartX=27.9965 StartY=107.79 StartZ=0 EndX=1.57905 EndY=122.295 EndZ=0
    g315: Circle CenterX=42.5666 CenterY=-67.3492 CenterZ=0 NormalX=0 NormalY=0 NormalZ=1 AngleXU=0 Radius=1
    g316: Circle CenterX=46.0728 CenterY=-65.424 CenterZ=0 NormalX=0 NormalY=0 NormalZ=1 AngleXU=0 Radius=1
    g317: Circle CenterX=46.0728 CenterY=-69.424 CenterZ=0 NormalX=0 NormalY=0 NormalZ=1 AngleXU=0 Radius=1
    g318: BSplineCurve PolesCount=3 KnotsCount=2 Degree=2 IsPeriodic=0
    g319: GeomPoint X=42.5666 Y=-67.3492 Z=0
    g320: GeomPoint X=46.0728 Y=-69.424 Z=0
    g321: Circle CenterX=46.0728 CenterY=-87.7794 CenterZ=0 NormalX=0 NormalY=0 NormalZ=1 AngleXU=0 Radius=1
    g322: Circle CenterX=46.0728 CenterY=-91.7794 CenterZ=0 NormalX=0 NormalY=0 NormalZ=1 AngleXU=0 Radius=1
    g323: Circle CenterX=42.0728 CenterY=-91.7794 CenterZ=0 NormalX=0 NormalY=0 NormalZ=1 AngleXU=0 Radius=1
    g324: BSplineCurve PolesCount=3 KnotsCount=2 Degree=2 IsPeriodic=0
    g325: GeomPoint X=46.0728 Y=-87.7794 Z=0
    g326: GeomPoint X=42.0728 Y=-91.7794 Z=0
    g327: Circle CenterX=2.07281 CenterY=-91.7794 CenterZ=0 NormalX=0 NormalY=0 NormalZ=1 AngleXU=0 Radius=1
    g328: Circle CenterX=-1.92719 CenterY=-91.7794 CenterZ=0 NormalX=0 NormalY=0 NormalZ=1 AngleXU=0 Radius=1
    g329: Circle CenterX=1.57905 CenterY=-89.8542 CenterZ=0 NormalX=0 NormalY=0 NormalZ=1 AngleXU=0 Radius=1
    g330: BSplineCurve PolesCount=3 KnotsCount=2 Degree=2 IsPeriodic=0
    g331: GeomPoint X=2.07281 Y=-91.7794 Z=0
    g332: GeomPoint X=1.57905 Y=-89.8542 Z=0
    g333: LineSegment StartX=2.07281 StartY=-91.7794 StartZ=0 EndX=42.0728 EndY=-91.7794 EndZ=0
    g334: LineSegment StartX=46.0728 StartY=-87.7794 StartZ=0 EndX=46.0728 EndY=-69.424 EndZ=0
    g335: LineSegment StartX=42.5666 StartY=-67.3492 StartZ=0 EndX=1.57905 EndY=-89.8542 EndZ=0
    g336: Circle CenterX=322.073 CenterY=76.4095 CenterZ=0 NormalX=0 NormalY=0 NormalZ=1 AngleXU=0 Radius=4
    g337: BSplineCurve PolesCount=3 KnotsCount=2 Degree=2 IsPeriodic=0
    g338: GeomPoint X=318.073 Y=72.4095 Z=0
    g339: GeomPoint X=322.073 Y=76.4095 Z=0
    g340: Circle CenterX=375.073 CenterY=72.4095 CenterZ=0 NormalX=0 NormalY=0 NormalZ=1 AngleXU=0 Radius=1
    g341: Circle CenterX=375.073 CenterY=76.4095 CenterZ=0 NormalX=0 NormalY=0 NormalZ=1 AngleXU=0 Radius=1
    g342: Circle CenterX=371.073 CenterY=76.4095 CenterZ=0 NormalX=0 NormalY=0 NormalZ=1 AngleXU=0 Radius=1
    g343: BSplineCurve PolesCount=3 KnotsCount=2 Degree=2 IsPeriodic=0
    g344: GeomPoint X=375.073 Y=72.4095 Z=0
    g345: GeomPoint X=371.073 Y=76.4095 Z=0
    g346: LineSegment StartX=322.073 StartY=76.4095 StartZ=0 EndX=371.073 EndY=76.4095 EndZ=0
    g347: LineSegment StartX=318.073 StartY=72.4095 StartZ=0 EndX=318.073 EndY=-47.4823 EndZ=0
    g348: LineSegment StartX=375.073 StartY=72.4095 StartZ=0 EndX=375.073 EndY=-78.7896 EndZ=0
    g349: ArcOfCircle CenterX=-26.9272 CenterY=22.1087 CenterZ=0 NormalX=0 NormalY=0 NormalZ=1 AngleXU=0 Radius=4 StartAngle=5e-16 EndAngle=3.14159
    g350: LineSegment StartX=-30.9272 StartY=22.1087 StartZ=0 EndX=-34.9272 EndY=-83.7794 EndZ=0
    g351: LineSegment StartX=-18.9272 StartY=-83.7794 StartZ=0 EndX=-22.9272 EndY=22.1087 EndZ=0
  constraints (576):
    c: Coincident(g0,g2)
    c: Block(g0)
    c: Block(g1)
    c: Vertical(g3)
    c: Vertical(g4)
    c: Block(g4)
    c: Block(g3)
    c: Tangent(g5,g8) = 1.5708
    c: Tangent(g5,g7) = -1.5708
    c: Tangent(g7,g6) = -1.5708
    c: Tangent(g8,g6) = 1.5708
    c: Vertical(g7)
    c: Equal(g5,g6)
    c: Block(g8)
    c: Block(g7)
    c: Tangent(g9,g10) = 1.5708
    c: Tangent(g10,g12) = 1.5708
    c: Equal(g9,g12)
    c: Coincident(g11,g9)
    c: Coincident(g11,g12)
    c: Block(g10)
    c: Block(g11)
    c: Weight(g13) = 1
    c: Equal(g13,g14)
    c: Equal(g13,g15)
    c: InternalAlignment(g13,g16)
    c: InternalAlignment(g14,g16)
    c: InternalAlignment(g15,g16)
    c: InternalAlignment(g17,g16)
    c: InternalAlignment(g18,g16)
    c: Weight(g19) = 1
    c: Equal(g19,g20)
    c: Equal(g19,g21)
    c: InternalAlignment(g19,g22)
    c: InternalAlignment(g20,g22)
    c: InternalAlignment(g21,g22)
    c: InternalAlignment(g23,g22)
    c: InternalAlignment(g24,g22)
    c: Block(g22)
    c: Block(g16)
    c: Weight(g25) = 1
    c: Equal(g25,g26)
    c: Equal(g25,g27)
    c: InternalAlignment(g25,g28)
    c: InternalAlignment(g26,g28)
    c: InternalAlignment(g27,g28)
    c: InternalAlignment(g29,g28)
    c: InternalAlignment(g30,g28)
    c: Weight(g31) = 1
    c: Equal(g31,g32)
    c: Equal(g31,g33)
    c: InternalAlignment(g31,g34)
    c: InternalAlignment(g32,g34)
    c: InternalAlignment(g33,g34)
    c: InternalAlignment(g35,g34)
    c: InternalAlignment(g36,g34)
    c: Block(g34)
    c: Block(g28)
    c: Weight(g37) = 1
    c: Equal(g37,g38)
    c: Equal(g37,g39)
    c: InternalAlignment(g37,g40)
    c: InternalAlignment(g38,g40)
    c: InternalAlignment(g39,g40)
    c: InternalAlignment(g41,g40)
    c: InternalAlignment(g42,g40)
    c: Weight(g43) = 1
    c: Equal(g43,g44)
    c: Equal(g43,g45)
    c: InternalAlignment(g43,g46)
    c: InternalAlignment(g44,g46)
    c: InternalAlignment(g45,g46)
    c: InternalAlignment(g47,g46)
    c: InternalAlignment(g48,g46)
    c: Block(g40)
    c: Block(g46)
    c: Coincident(g49,g4)
    c: Coincident(g49,g3)
    c: Horizontal(g49)
    c: Distance(g49) = 450
    c: Coincident(g50,g4)
    c: Coincident(g50,g3)
    c: Horizontal(g50)
    c: Horizontal(g51)
    c: Coincident(g2,g51)
    c: Block(g51)
    c: Coincident(g1,g51)
    c: Weight(g52) = 1
    c: Equal(g52,g53)
    c: Equal(g52,g54)
    c: InternalAlignment(g52,g55)
    c: InternalAlignment(g53,g55)
    c: InternalAlignment(g54,g55)
    c: InternalAlignment(g56,g55)
    c: InternalAlignment(g57,g55)
    c: Block(g55)
    c: Weight(g58) = 1
    c: Equal(g58,g59)
    c: Equal(g58,g60)
    c: InternalAlignment(g58,g61)
    c: InternalAlignment(g59,g61)
    c: InternalAlignment(g60,g61)
    c: InternalAlignment(g62,g61)
    c: InternalAlignment(g63,g61)
    c: Block(g61)
    c: Weight(g64) = 1
    c: Equal(g64,g65)
    c: Equal(g64,g66)
    c: InternalAlignment(g64,g67)
    c: InternalAlignment(g65,g67)
    c: InternalAlignment(g66,g67)
    c: InternalAlignment(g68,g67)
    c: InternalAlignment(g69,g67)
    c: Block(g67)
    c: Weight(g70) = 1
    c: Equal(g70,g71)
    c: Equal(g70,g72)
    c: InternalAlignment(g70,g73)
    c: InternalAlignment(g71,g73)
    c: InternalAlignment(g72,g73)
    c: InternalAlignment(g74,g73)
    c: InternalAlignment(g75,g73)
    c: Block(g73)
    c: Weight(g76) = 1
    c: Equal(g76,g77)
    c: Equal(g76,g78)
    c: InternalAlignment(g76,g79)
    c: InternalAlignment(g77,g79)
    c: InternalAlignment(g78,g79)
    c: InternalAlignment(g80,g79)
    c: InternalAlignment(g81,g79)
    c: Weight(g82) = 1
    c: Equal(g82,g83)
    c: Equal(g82,g84)
    c: InternalAlignment(g82,g85)
    c: InternalAlignment(g83,g85)
    c: InternalAlignment(g84,g85)
    c: InternalAlignment(g86,g85)
    c: InternalAlignment(g87,g85)
    c: Block(g79)
    c: Block(g85)
    c: Coincident(g88,g79)
    c: Coincident(g88,g85)
    c: Vertical(g88)
    c: Coincident(g89,g79)
    c: Coincident(g89,g61)
    c: Coincident(g90,g61)
    c: Coincident(g90,g85)
    c: Weight(g91) = 1
    c: Equal(g91,g92)
    c: Equal(g91,g93)
    c: InternalAlignment(g91,g94)
    c: InternalAlignment(g92,g94)
    c: InternalAlignment(g93,g94)
    c: InternalAlignment(g95,g94)
    c: InternalAlignment(g96,g94)
    c: Weight(g97) = 1
    c: Equal(g97,g98)
    c: Equal(g97,g99)
    c: InternalAlignment(g97,g100)
    c: InternalAlignment(g98,g100)
    c: InternalAlignment(g99,g100)
    c: InternalAlignment(g101,g100)
    c: InternalAlignment(g102,g100)
    c: Block(g94)
    c: Block(g100)
    c: Coincident(g103,g94)
    c: Coincident(g103,g100)
    c: Vertical(g103)
    c: Coincident(g104,g94)
    c: Coincident(g104,g55)
    c: Coincident(g105,g55)
    c: Coincident(g105,g100)
    c: Weight(g106) = 1
    c: Equal(g106,g107)
    c: Equal(g106,g108)
    c: InternalAlignment(g106,g109)
    c: InternalAlignment(g107,g109)
    c: InternalAlignment(g108,g109)
    c: InternalAlignment(g110,g109)
    c: InternalAlignment(g111,g109)
    c: Weight(g112) = 1
    c: Equal(g112,g113)
    c: Equal(g112,g114)
    c: InternalAlignment(g112,g115)
    c: InternalAlignment(g113,g115)
    c: InternalAlignment(g114,g115)
    c: InternalAlignment(g116,g115)
    c: InternalAlignment(g117,g115)
    c: Block(g109)
    c: Block(g115)
    c: Coincident(g118,g109)
    c: Coincident(g118,g115)
    c: Vertical(g118)
    c: Coincident(g119,g115)
    c: Coincident(g119,g73)
    c: Coincident(g120,g73)
    c: Coincident(g120,g109)
    c: Weight(g121) = 1
    c: Equal(g121,g122)
    c: Equal(g121,g123)
    c: InternalAlignment(g121,g124)
    c: InternalAlignment(g122,g124)
    c: InternalAlignment(g123,g124)
    c: InternalAlignment(g125,g124)
    c: InternalAlignment(g126,g124)
    c: Weight(g127) = 1
    c: Equal(g127,g128)
    c: Equal(g127,g129)
    c: InternalAlignment(g127,g130)
    c: InternalAlignment(g128,g130)
    c: InternalAlignment(g129,g130)
    c: InternalAlignment(g131,g130)
    c: InternalAlignment(g132,g130)
    c: Block(g124)
    c: Block(g130)
    c: Coincident(g133,g124)
    c: Coincident(g133,g130)
    c: Vertical(g133)
    c: Coincident(g134,g130)
    c: Coincident(g134,g67)
    c: Coincident(g135,g67)
    c: Coincident(g135,g124)
    c: Weight(g136) = 1
    c: Equal(g136,g137)
    c: Equal(g136,g138)
    c: InternalAlignment(g136,g139)
    c: InternalAlignment(g137,g139)
    c: InternalAlignment(g138,g139)
    c: InternalAlignment(g140,g139)
    c: InternalAlignment(g141,g139)
    c: Weight(g142) = 1
    c: Equal(g142,g143)
    c: Equal(g142,g144)
    c: InternalAlignment(g142,g145)
    c: InternalAlignment(g143,g145)
    c: InternalAlignment(g144,g145)
    c: InternalAlignment(g146,g145)
    c: InternalAlignment(g147,g145)
    c: Weight(g148) = 1
    c: Equal(g148,g149)
    c: Equal(g148,g150)
    c: InternalAlignment(g148,g151)
    c: InternalAlignment(g149,g151)
    c: InternalAlignment(g150,g151)
    c: InternalAlignment(g152,g151)
    c: InternalAlignment(g153,g151)
    c: Weight(g154) = 1
    c: Equal(g154,g155)
    c: Equal(g154,g156)
    c: InternalAlignment(g154,g157)
    c: InternalAlignment(g155,g157)
    c: InternalAlignment(g156,g157)
    c: InternalAlignment(g158,g157)
    c: InternalAlignment(g159,g157)
    c: Block(g157)
    c: Block(g151)
    c: Block(g145)
    c: Block(g139)
    c: Coincident(g160,g34)
    c: Coincident(g160,g157)
    c: Coincident(g161,g157)
    c: Coincident(g161,g151)
    c: Horizontal(g161)
    c: Coincident(g162,g151)
    c: Coincident(g162,g34)
    c: Vertical(g162)
    c: Coincident(g163,g28)
    c: Coincident(g163,g145)
    c: Vertical(g163)
    c: Coincident(g164,g145)
    c: Coincident(g164,g139)
    c: Horizontal(g164)
    c: Coincident(g165,g139)
    c: Coincident(g165,g28)
    c: Weight(g166) = 1
    c: Equal(g166,g167)
    c: Equal(g166,g168)
    c: InternalAlignment(g166,g169)
    c: InternalAlignment(g167,g169)
    c: InternalAlignment(g168,g169)
    c: InternalAlignment(g170,g169)
    c: InternalAlignment(g171,g169)
    c: Weight(g172) = 1
    c: Equal(g172,g173)
    c: Equal(g172,g174)
    c: InternalAlignment(g172,g175)
    c: InternalAlignment(g173,g175)
    c: InternalAlignment(g174,g175)
    c: InternalAlignment(g176,g175)
    c: InternalAlignment(g177,g175)
    c: Weight(g178) = 1
    c: Equal(g178,g179)
    c: Equal(g178,g180)
    c: InternalAlignment(g178,g181)
    c: InternalAlignment(g179,g181)
    c: InternalAlignment(g180,g181)
    c: InternalAlignment(g182,g181)
    c: InternalAlignment(g183,g181)
    c: Weight(g184) = 1
    c: Equal(g184,g185)
    c: Equal(g184,g186)
    c: InternalAlignment(g184,g187)
    c: InternalAlignment(g185,g187)
    c: InternalAlignment(g186,g187)
    c: InternalAlignment(g188,g187)
    c: InternalAlignment(g189,g187)
    c: Block(g187)
    c: Block(g181)
    c: Block(g175)
    c: Block(g169)
    c: Coincident(g190,g187)
    c: Coincident(g190,g181)
    c: Horizontal(g190)
    c: Coincident(g191,g181)
    c: Coincident(g191,g16)
    c: Vertical(g191)
    c: Coincident(g192,g22)
    c: Coincident(g192,g175)
    c: Vertical(g192)
    c: Coincident(g193,g175)
    c: Coincident(g193,g169)
    c: Horizontal(g193)
    c: Coincident(g194,g169)
    c: Coincident(g194,g22)
    c: Coincident(g195,g16)
    c: Weight(g196) = 1
    c: Equal(g196,g197)
    c: Equal(g196,g198)
    c: InternalAlignment(g196,g199)
    c: InternalAlignment(g197,g199)
    c: InternalAlignment(g198,g199)
    c: InternalAlignment(g200,g199)
    c: InternalAlignment(g201,g199)
    c: Weight(g202) = 1
    c: Equal(g202,g203)
    c: Equal(g202,g204)
    c: InternalAlignment(g202,g205)
    c: InternalAlignment(g203,g205)
    c: InternalAlignment(g204,g205)
    c: InternalAlignment(g206,g205)
    c: InternalAlignment(g207,g205)
    c: Block(g205)
    c: Block(g199)
    c: Coincident(g208,g205)
    c: Coincident(g208,g40)
    c: Coincident(g209,g40)
    c: Coincident(g209,g199)
    c: Coincident(g210,g199)
    c: Coincident(g210,g205)
    c: Vertical(g210)
    c: Weight(g211) = 1
    c: Equal(g211,g212)
    c: Equal(g211,g213)
    c: InternalAlignment(g211,g214)
    c: InternalAlignment(g212,g214)
    c: InternalAlignment(g213,g214)
    c: InternalAlignment(g215,g214)
    c: InternalAlignment(g216,g214)
    c: Weight(g217) = 1
    c: Equal(g217,g218)
    c: Equal(g217,g219)
    c: InternalAlignment(g217,g220)
    c: InternalAlignment(g218,g220)
    c: InternalAlignment(g219,g220)
    c: InternalAlignment(g221,g220)
    c: InternalAlignment(g222,g220)
    c: Block(g220)
    c: Block(g214)
    c: Coincident(g223,g214)
    c: Coincident(g223,g46)
    c: Coincident(g224,g46)
    c: Coincident(g224,g220)
    c: Coincident(g225,g220)
    c: Coincident(g225,g214)
    c: Vertical(g225)
    c: Horizontal(g226)
    c: Block(g226)
    c: Vertical(g227)
    c: Block(g227)
    c: Block(g228)
    c: Weight(g229) = 1
    c: Equal(g229,g230)
    c: Equal(g229,g231)
    c: InternalAlignment(g229,g232)
    c: InternalAlignment(g230,g232)
    c: InternalAlignment(g231,g232)
    c: InternalAlignment(g233,g232)
    c: InternalAlignment(g234,g232)
    c: Weight(g235) = 1
    c: Equal(g235,g236)
    c: Equal(g235,g237)
    c: InternalAlignment(g235,g238)
    c: InternalAlignment(g236,g238)
    c: InternalAlignment(g237,g238)
    c: InternalAlignment(g239,g238)
    c: InternalAlignment(g240,g238)
    c: Weight(g241) = 1
    c: Equal(g241,g242)
    c: Equal(g241,g243)
    c: InternalAlignment(g241,g244)
    c: InternalAlignment(g242,g244)
    c: InternalAlignment(g243,g244)
    c: InternalAlignment(g245,g244)
    c: InternalAlignment(g246,g244)
    c: Weight(g247) = 1
    c: Equal(g247,g248)
    c: Equal(g247,g249)
    c: InternalAlignment(g247,g250)
    c: InternalAlignment(g248,g250)
    c: InternalAlignment(g249,g250)
    c: InternalAlignment(g251,g250)
    c: InternalAlignment(g252,g250)
    c: Block(g232)
    c: Block(g238)
    c: Block(g244)
    c: Block(g250)
    c: Coincident(g253,g238)
    c: Coincident(g253,g232)
    c: Horizontal(g253)
    c: Block(g195)
    c: Weight(g254) = 1
    c: Equal(g254,g255)
    c: Equal(g254,g256)
    c: InternalAlignment(g254,g257)
    c: InternalAlignment(g255,g257)
    c: InternalAlignment(g256,g257)
    c: InternalAlignment(g258,g257)
    c: InternalAlignment(g259,g257)
    c: Weight(g260) = 1
    c: Equal(g260,g261)
    c: Equal(g260,g262)
    c: InternalAlignment(g260,g263)
    c: InternalAlignment(g261,g263)
    c: InternalAlignment(g262,g263)
    c: InternalAlignment(g264,g263)
    c: InternalAlignment(g265,g263)
    c: Block(g257)
    c: Block(g263)
    c: Coincident(g266,g257)
    c: Coincident(g266,g263)
    c: Weight(g267) = 1
    c: Equal(g267,g268)
    c: Equal(g267,g269)
    c: InternalAlignment(g267,g270)
    c: InternalAlignment(g268,g270)
    c: InternalAlignment(g269,g270)
    c: InternalAlignment(g271,g270)
    c: InternalAlignment(g272,g270)
    c: Weight(g273) = 1
    c: Equal(g273,g274)
    c: Equal(g273,g275)
    c: InternalAlignment(g273,g276)
    c: InternalAlignment(g274,g276)
    c: InternalAlignment(g275,g276)
    c: InternalAlignment(g277,g276)
    c: InternalAlignment(g278,g276)
    c: Weight(g279) = 1
    c: Equal(g279,g280)
    c: Equal(g279,g281)
    c: InternalAlignment(g279,g282)
    c: InternalAlignment(g280,g282)
    c: InternalAlignment(g281,g282)
    c: InternalAlignment(g283,g282)
    c: InternalAlignment(g284,g282)
    c: Block(g282)
    c: Block(g276)
    c: Block(g270)
    c: Coincident(g285,g276)
    c: Coincident(g285,g270)
    c: Coincident(g286,g270)
    c: Coincident(g286,g282)
    c: Vertical(g286)
    c: Coincident(g287,g282)
    c: Coincident(g287,g276)
    c: Horizontal(g287)
    c: Weight(g288) = 1
    c: Equal(g288,g289)
    c: InternalAlignment(g288,g290)
    c: InternalAlignment(g289,g290)
    c: InternalAlignment(g291,g290)
    c: InternalAlignment(g292,g290)
    c: Weight(g293) = 1
    c: InternalAlignment(g294,g296)
    c: InternalAlignment(g295,g296)
    c: InternalAlignment(g297,g296)
    c: InternalAlignment(g298,g296)
    c: Weight(g299) = 1
    c: Equal(g299,g300)
    c: Equal(g299,g301)
    c: InternalAlignment(g299,g302)
    c: InternalAlignment(g300,g302)
    c: InternalAlignment(g301,g302)
    c: InternalAlignment(g303,g302)
    c: InternalAlignment(g304,g302)
    c: Equal(g305,g306)
    c: Equal(g305,g307)
    c: InternalAlignment(g305,g308)
    c: InternalAlignment(g306,g308)
    c: InternalAlignment(g307,g308)
    c: InternalAlignment(g309,g308)
    c: InternalAlignment(g310,g308)
    c: Block(g296)
    c: Block(g302)
    c: Block(g308)
    c: Block(g290)
    c: Coincident(g311,g290)
    c: Coincident(g311,g296)
    c: Horizontal(g311)
    c: Coincident(g312,g296)
    c: Coincident(g312,g302)
    c: Vertical(g312)
    c: Coincident(g313,g302)
    c: Coincident(g313,g308)
    c: Horizontal(g313)
    c: Coincident(g314,g308)
    c: Coincident(g314,g290)
    c: Weight(g315) = 1
    c: Equal(g315,g316)
    c: Equal(g315,g317)
    c: InternalAlignment(g315,g318)
    c: InternalAlignment(g316,g318)
    c: InternalAlignment(g317,g318)
    c: InternalAlignment(g319,g318)
    c: InternalAlignment(g320,g318)
    c: Weight(g321) = 1
    c: Equal(g321,g322)
    c: Equal(g321,g323)
    c: InternalAlignment(g321,g324)
    c: InternalAlignment(g322,g324)
    c: InternalAlignment(g323,g324)
    c: InternalAlignment(g325,g324)
    c: InternalAlignment(g326,g324)
    c: Weight(g327) = 1
    c: Equal(g327,g328)
    c: Equal(g327,g329)
    c: InternalAlignment(g327,g330)
    c: InternalAlignment(g328,g330)
    c: InternalAlignment(g329,g330)
    c: InternalAlignment(g331,g330)
    c: InternalAlignment(g332,g330)
    c: Block(g330)
    c: Block(g324)
    c: Block(g318)
    c: Coincident(g333,g330)
    c: Coincident(g333,g324)
    c: Horizontal(g333)
    c: Coincident(g334,g324)
    c: Coincident(g334,g318)
    c: Vertical(g334)
    c: Coincident(g335,g318)
    c: Coincident(g335,g330)
    c: InternalAlignment(g336,g337)
    c: InternalAlignment(g338,g337)
    c: InternalAlignment(g339,g337)
    c: Block(g337)
    c: Equal(g340,g341)
    c: Equal(g340,g342)
    c: InternalAlignment(g340,g343)
    c: InternalAlignment(g341,g343)
    c: InternalAlignment(g342,g343)
    c: InternalAlignment(g344,g343)
    c: InternalAlignment(g345,g343)
    c: Block(g343)
    c: Coincident(g346,g337)
    c: Horizontal(g346)
    c: Block(g346)
    c: Coincident(g347,g337)
    c: Coincident(g347,g263)
    c: Vertical(g347)
    c: Coincident(g348,g343)
    c: Coincident(g348,g257)
    c: Vertical(g348)
    c: Coincident(g349,g5)
    c: Coincident(g350,g6)
    c: Coincident(g351,g6)
FEATURE [Sketcher::SketchObject] Sketch001
  FullyConstrained = true
  MapMode = 4
  Placement = pos=(0,0,0) rot=(0.57735,0.57735,0.57735;2.0944rad)
  Support = -> [Sketch]
  sketch-geometry (46):
    g0: BSplineCurve PolesCount=3 KnotsCount=2 Degree=2 IsPeriodic=0
    g1: ArcOfCircle CenterX=73.1223 CenterY=-32.291 CenterZ=0 NormalX=0 NormalY=0 NormalZ=1 AngleXU=0 Radius=13 StartAngle=5.92268 EndAngle=9.06428
    g2: ArcOfCircle CenterX=66.7816 CenterY=-49.1439 CenterZ=0 NormalX=0 NormalY=0 NormalZ=1 AngleXU=0 Radius=13 StartAngle=2.78068 EndAngle=5.92131
    g3: ArcOfCircle CenterX=55.9263 CenterY=-78.1807 CenterZ=0 NormalX=0 NormalY=0 NormalZ=1 AngleXU=0 Radius=13 StartAngle=5.92268 EndAngle=9.06428
    g4: ArcOfCircle CenterX=49.5884 CenterY=-95.0342 CenterZ=0 NormalX=0 NormalY=0 NormalZ=1 AngleXU=0 Radius=13 StartAngle=2.78068 EndAngle=5.92131
    g5: ArcOfCircle CenterX=38.7206 CenterY=-124.067 CenterZ=0 NormalX=0 NormalY=0 NormalZ=1 AngleXU=0 Radius=13 StartAngle=5.92268 EndAngle=9.06428
    g6: ArcOfCircle CenterX=32.3875 CenterY=-140.92 CenterZ=0 NormalX=0 NormalY=0 NormalZ=1 AngleXU=0 Radius=13 StartAngle=2.78068 EndAngle=5.92131
    g7: ArcOfCircle CenterX=21.4715 CenterY=-169.934 CenterZ=0 NormalX=0 NormalY=0 NormalZ=1 AngleXU=0 Radius=13 StartAngle=5.92268 EndAngle=9.06428
    g8: ArcOfCircle CenterX=15.1336 CenterY=-186.787 CenterZ=0 NormalX=0 NormalY=0 NormalZ=1 AngleXU=0 Radius=13 StartAngle=2.78068 EndAngle=5.92131
    g9-g12: Circle x4 (B-spline internal-alignment scaffolding for g13; pole/knot coordinates omitted)
    g13: BSplineCurve PolesCount=4 KnotsCount=2 Degree=3 IsPeriodic=0
    g14: GeomPoint X=28.8094 Y=-19.0875 Z=0
    g15: GeomPoint X=47.0443 Y=-50.4712 Z=0
    g16: Circle CenterX=53.5586 CenterY=-23.2695 CenterZ=0 NormalX=0 NormalY=0 NormalZ=1 AngleXU=0 Radius=3.24518
    g17: Circle CenterX=-195.441 CenterY=-127.082 CenterZ=0 NormalX=0 NormalY=0 NormalZ=1 AngleXU=0 Radius=1
    g18: Circle CenterX=-8.24091 CenterY=-197.481 CenterZ=0 NormalX=0 NormalY=0 NormalZ=1 AngleXU=0 Radius=1
    g19: Circle CenterX=12.8789 CenterY=-141.321 CenterZ=0 NormalX=0 NormalY=0 NormalZ=1 AngleXU=0 Radius=1
    g20: BSplineCurve PolesCount=3 KnotsCount=2 Degree=2 IsPeriodic=0
    g21: GeomPoint X=-195.441 Y=-127.082 Z=0
    g22: GeomPoint X=12.8789 Y=-141.321 Z=0
    g23: Circle CenterX=-12.8016 CenterY=-179.036 CenterZ=0 NormalX=0 NormalY=0 NormalZ=1 AngleXU=0 Radius=10.5072
    g24: Circle CenterX=0.933922 CenterY=-166.43 CenterZ=0 NormalX=0 NormalY=0 NormalZ=1 AngleXU=0 Radius=3.26661
    g25: Circle CenterX=-33.5518 CenterY=-176.44 CenterZ=0 NormalX=0 NormalY=0 NormalZ=1 AngleXU=0 Radius=5.64388
    g26: Circle CenterX=-47.2366 CenterY=-173.859 CenterZ=0 NormalX=0 NormalY=0 NormalZ=1 AngleXU=0 Radius=3.01653
    g27: Circle CenterX=-56.2595 CenterY=-171.456 CenterZ=0 NormalX=0 NormalY=0 NormalZ=1 AngleXU=0 Radius=2.12826
    g28: ArcOfCircle CenterX=51.2151 CenterY=-198.473 CenterZ=0 NormalX=0 NormalY=0 NormalZ=1 AngleXU=0 Radius=20 StartAngle=2.78189 EndAngle=4.35269
    g29: LineSegment StartX=32.4951 StartY=-191.433 StartZ=0 EndX=94.6578 EndY=-26.1352 EndZ=0
    g30: LineSegment StartX=43.1192 StartY=-220.001 StartZ=0 EndX=-196.497 EndY=-129.89 EndZ=0
    g31: LineSegment StartX=43.1192 StartY=-220.001 StartZ=0 EndX=44.1752 EndY=-217.193 EndZ=0
    g32: LineSegment StartX=117.223 StartY=-19.0875 StartZ=0 EndX=117.223 EndY=-16.0875 EndZ=0
    g33: LineSegment StartX=117.223 StartY=-16.0875 StartZ=0 EndX=17.2232 EndY=-16.0875 EndZ=0
    g34: LineSegment StartX=17.2232 StartY=-16.0875 StartZ=0 EndX=17.2232 EndY=-19.0875 EndZ=0
    g35: LineSegment StartX=28.8094 StartY=-19.0875 StartZ=0 EndX=17.2232 EndY=-19.0875 EndZ=0
    g36: LineSegment StartX=47.0443 StartY=-50.4712 StartZ=0 EndX=12.8789 EndY=-141.321 EndZ=0
    g37: LineSegment StartX=-195.441 StartY=-127.082 StartZ=0 EndX=-196.497 EndY=-129.89 EndZ=0
    g38: LineSegment StartX=85.2866 StartY=-36.8766 StartZ=0 EndX=78.9396 EndY=-53.7463 EndZ=0
    g39: LineSegment StartX=60.9579 StartY=-27.7053 StartZ=0 EndX=54.6191 EndY=-44.5532 EndZ=0
    g40: LineSegment StartX=68.0907 StartY=-82.7664 StartZ=0 EndX=61.7465 EndY=-99.6365 EndZ=0
    g41: LineSegment StartX=43.7619 StartY=-73.595 StartZ=0 EndX=37.426 EndY=-90.4435 EndZ=0
    g42: LineSegment StartX=50.885 StartY=-128.652 StartZ=0 EndX=44.5456 EndY=-145.522 EndZ=0
    g43: LineSegment StartX=26.5562 StartY=-119.481 StartZ=0 EndX=20.2251 EndY=-136.329 EndZ=0
    g44: LineSegment StartX=9.3071 StartY=-165.349 StartZ=0 EndX=2.97115 EndY=-182.197 EndZ=0
    g45: LineSegment StartX=33.6358 StartY=-174.52 StartZ=0 EndX=27.2917 EndY=-191.39 EndZ=0
  constraints (71):
    c: Block(g0)
    c: Block(g1)
    c: Block(g2)
    c: Block(g4)
    c: Block(g3)
    c: Block(g6)
    c: Block(g5)
    c: Block(g8)
    c: Block(g7)
    c: Weight(g9) = 1
    c: Equal(g9,g10)
    c: Equal(g9,g11)
    c: Equal(g9,g12)
    c: InternalAlignment(g9-g12 -> g13) x4
    c: InternalAlignment(g14,g13)
    c: InternalAlignment(g15,g13)
    c: Block(g16)
    c: Weight(g17) = 1
    c: Equal(g17,g18)
    c: Equal(g17,g19)
    c: InternalAlignment(g17,g20)
    c: InternalAlignment(g18,g20)
    c: InternalAlignment(g19,g20)
    c: InternalAlignment(g21,g20)
    c: InternalAlignment(g22,g20)
    c: Block(g20)
    c: Block(g23)
    c: Block(g24)
    c: Block(g25)
    c: Block(g26)
    c: Block(g27)
    c: Block(g28)
    c: Coincident(g29,g28)
    c: Coincident(g29,g0)
    c: Block(g13)
    c: Coincident(g31,g30)
    c: Coincident(g31,g28)
    c: Block(g31)
    c: Coincident(g32,g0)
    c: Vertical(g32)
    c: Coincident(g33,g32)
    c: Horizontal(g33)
    c: Coincident(g34,g33)
    c: Vertical(g34)
    c: Block(g33)
    c: Coincident(g35,g13)
    c: Coincident(g35,g34)
    c: Horizontal(g35)
    c: Coincident(g36,g13)
    c: Coincident(g36,g20)
    c: Coincident(g37,g20)
    c: Coincident(g37,g30)
    c: Block(g30)
    c: Coincident(g38,g1)
    c: Coincident(g38,g2)
    c: Coincident(g39,g1)
    c: Coincident(g39,g2)
    c: Coincident(g40,g3)
    c: Coincident(g40,g4)
    c: Coincident(g41,g3)
    c: Coincident(g41,g4)
    c: Coincident(g42,g5)
    c: Coincident(g42,g6)
    c: Coincident(g43,g5)
    c: Coincident(g43,g6)
    c: Coincident(g44,g7)
    c: Coincident(g44,g8)
    c: Coincident(g45,g7)
    c: Coincident(g45,g8)
    c: Distance(g30) = 256
    c: Distance(g33) = 100
FEATURE [Part::Extrusion] Extrude002
  Base = -> Sketch001
  Dir = (1,0,0)
  DirMode = 2
  FaceMakerClass = Part::FaceMakerBullseye
  LengthFwd = 8
  LengthRev = 0
  Solid = true
  Symmetric = false
FEATURE [Sketcher::SketchObject] Sketch002
  FullyConstrained = true
  sketch-geometry (20):
    g0: LineSegment StartX=-2.77179 StartY=-200.304 StartZ=0 EndX=5.22821 EndY=-200.304 EndZ=0
    g1: LineSegment StartX=5.22821 StartY=-200.304 StartZ=0 EndX=5.22821 EndY=-197.304 EndZ=0
    g2: LineSegment StartX=-2.77179 StartY=-200.304 StartZ=0 EndX=-2.77179 EndY=-197.304 EndZ=0
    g3: LineSegment StartX=5.22821 StartY=-197.304 StartZ=0 EndX=8.22821 EndY=-197.304 EndZ=0
    g4: LineSegment StartX=-2.77179 StartY=-197.304 StartZ=0 EndX=-5.77179 EndY=-197.304 EndZ=0
    g5: LineSegment StartX=19.2282 StartY=-203.304 StartZ=0 EndX=19.2282 EndY=-206.304 EndZ=0
    g6: LineSegment StartX=-16.7718 StartY=-203.304 StartZ=0 EndX=-16.7718 EndY=-206.304 EndZ=0
    g7: LineSegment StartX=-16.7718 StartY=-206.304 StartZ=0 EndX=19.2282 EndY=-206.304 EndZ=0
    g8: Circle CenterX=-16.7718 CenterY=-203.304 CenterZ=0 NormalX=0 NormalY=0 NormalZ=1 AngleXU=0 Radius=1
    g9: Circle CenterX=-5.77179 CenterY=-203.304 CenterZ=0 NormalX=0 NormalY=0 NormalZ=1 AngleXU=0 Radius=1
    g10: Circle CenterX=-5.77179 CenterY=-197.304 CenterZ=0 NormalX=0 NormalY=0 NormalZ=1 AngleXU=0 Radius=1
    g11: BSplineCurve PolesCount=3 KnotsCount=2 Degree=2 IsPeriodic=0
    g12: GeomPoint X=-16.7718 Y=-203.304 Z=0
    g13: GeomPoint X=-5.77179 Y=-197.304 Z=0
    g14: Circle CenterX=19.2282 CenterY=-203.304 CenterZ=0 NormalX=0 NormalY=0 NormalZ=1 AngleXU=0 Radius=1
    g15: Circle CenterX=8.22821 CenterY=-203.304 CenterZ=0 NormalX=0 NormalY=0 NormalZ=1 AngleXU=0 Radius=1
    g16: Circle CenterX=8.22821 CenterY=-197.304 CenterZ=0 NormalX=0 NormalY=0 NormalZ=1 AngleXU=0 Radius=1
    g17: BSplineCurve PolesCount=3 KnotsCount=2 Degree=2 IsPeriodic=0
    g18: GeomPoint X=19.2282 Y=-203.304 Z=0
    g19: GeomPoint X=8.22821 Y=-197.304 Z=0
  constraints (41):
    c: Horizontal(g0)
    c: Distance(g0) = 8
    c: Coincident(g1,g0)
    c: Vertical(g1)
    c: Distance(g1) = 3
    c: Coincident(g2,g0)
    c: Vertical(g2)
    c: Distance(g2) = 3
    c: Coincident(g3,g1)
    c: Horizontal(g3)
    c: Distance(g3) = 3
    c: Coincident(g4,g2)
    c: Horizontal(g4)
    c: Distance(g4) = 3
    c: Vertical(g5)
    c: Vertical(g6)
    c: Coincident(g7,g6)
    c: Coincident(g7,g5)
    c: Weight(g8) = 1
    c: Equal(g8,g9)
    c: Equal(g8,g10)
    c: Coincident(g11,g4)
    c: InternalAlignment(g8,g11)
    c: InternalAlignment(g9,g11)
    c: InternalAlignment(g10,g11)
    c: InternalAlignment(g12,g11)
    c: InternalAlignment(g13,g11)
    c: Coincident(g17,g5)
    c: Weight(g14) = 1
    c: Equal(g14,g15)
    c: Equal(g14,g16)
    c: Coincident(g17,g3)
    c: InternalAlignment(g14,g17)
    c: InternalAlignment(g15,g17)
    c: InternalAlignment(g16,g17)
    c: InternalAlignment(g18,g17)
    c: InternalAlignment(g19,g17)
    c: Block(g7)
    c: Block(g17)
    c: Block(g11)
    c: Block(g6)
FEATURE [Part::Extrusion] Extrude003
  Base = -> Sketch002
  Dir = (0,0,1)
  DirMode = 2
  FaceMakerClass = Part::FaceMakerBullseye
  LengthFwd = 260
  LengthRev = 0
  Solid = true
  Symmetric = false
FEATURE [Part::Extrusion] Extrude
  Base = -> Sketch
  Dir = (0,0,1)
  DirMode = 2
  FaceMakerClass = Part::FaceMakerBullseye
  LengthFwd = 14
  LengthRev = 0
  Solid = true
  Symmetric = false
